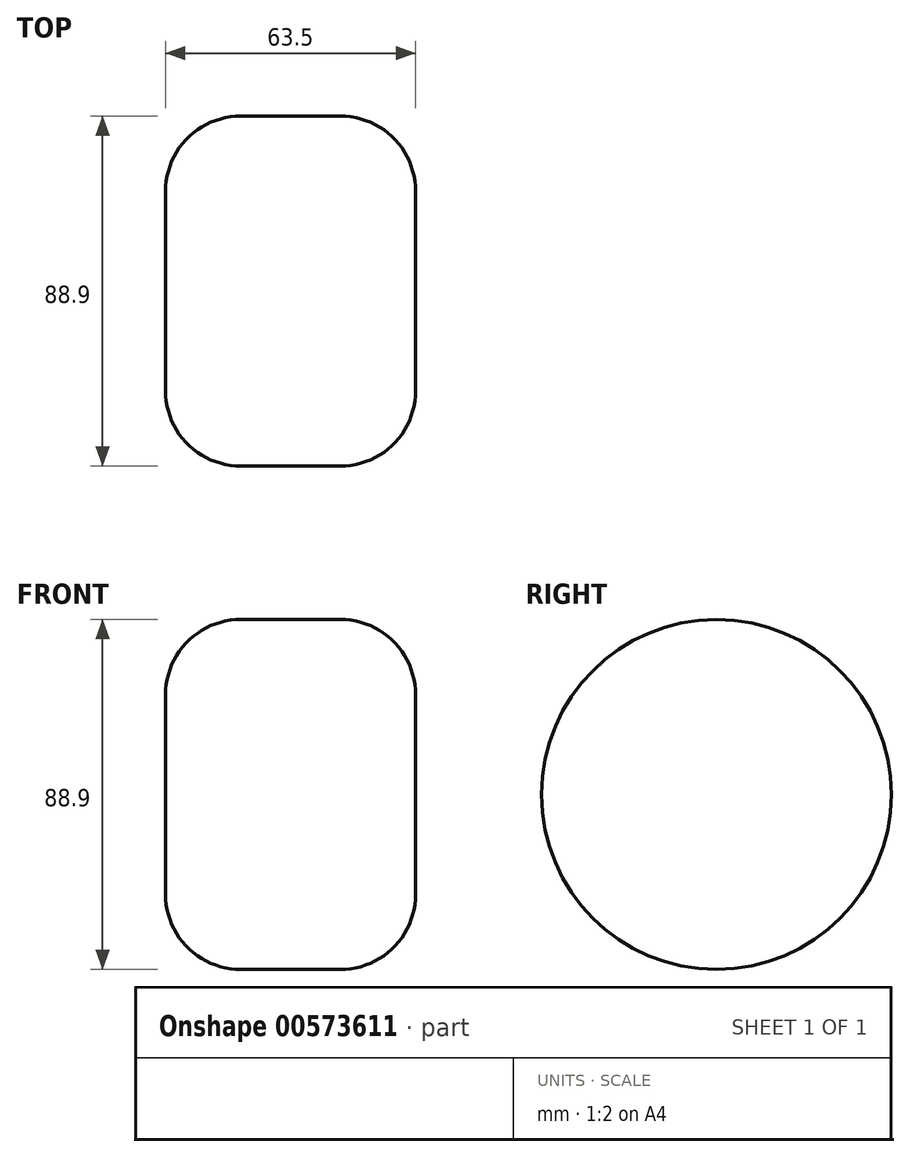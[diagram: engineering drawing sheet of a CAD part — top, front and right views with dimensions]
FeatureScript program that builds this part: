
annotation { "Feature Type Name" : "Feature", "Feature Type Description" : "" }
export const myFeature = defineFeature(function(context is Context, id is Id, definition is map)
    precondition{}
    {
        {
            var Q0;
            Q0=qCreatedBy(makeId("Front.planeOp"),FACE);
            var sketch = newSketch(context, id + "F0", { "sketchPlane" : qUnion([Q0])});
            skLineSegment(sketch, "E0", {"start": v(0, 44.45) * mm, "end": v(12.7, 44.45) * mm});
            skArc(sketch, "E1", {"start": v(12.7, 44.45) * mm, "mid": v(26.17, 38.87) * mm, "end": v(31.75, 25.4) * mm});
            skLineSegment(sketch, "E2", {"start": v(31.75, 25.4) * mm, "end": v(31.75, 0) * mm});
            skLineSegment(sketch, "E3", {"start": v(31.75, 0) * mm, "end": v(0, 0) * mm});
            skLineSegment(sketch, "E4", {"start": v(0, 0) * mm, "end": v(-31.75, 0) * mm});
            skLineSegment(sketch, "E5", {"start": v(-31.75, 0) * mm, "end": v(-31.75, 25.4) * mm});
            skLineSegment(sketch, "E6", {"start": v(0, 44.45) * mm, "end": v(-12.7, 44.45) * mm});
            skArc(sketch, "E7", {"start": v(-31.75, 25.4) * mm, "mid": v(-26.17, 38.87) * mm, "end": v(-12.7, 44.45) * mm});
            skSolve(sketch);
        }
        {
            var Q0;
            Q0 = qSketchRegion(id + "F0", true);
            var Q1;
            Q1=sQuery(id+"F0.wireOp",EDGE,"E4");
            revolve(context, id + "F1", {"entities" : qUnion([Q0]), "axis" : qUnion([Q1]), "revolveType" : RevolveType.FULL});
        }
    });
